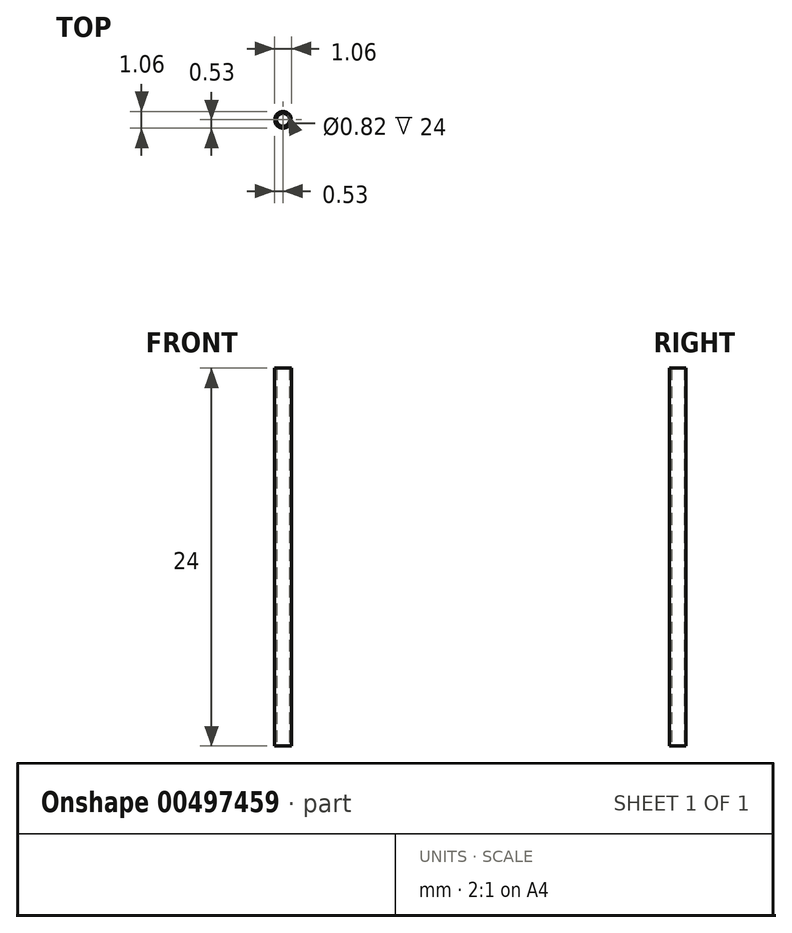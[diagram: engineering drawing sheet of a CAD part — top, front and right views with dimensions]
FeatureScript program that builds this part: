
annotation { "Feature Type Name" : "Feature", "Feature Type Description" : "" }
export const myFeature = defineFeature(function(context is Context, id is Id, definition is map)
    precondition{}
    {
        {
            var Q0;
            Q0=qCreatedBy(makeId("Top.planeOp"),FACE);
            var sketch = newSketch(context, id + "F0", { "sketchPlane" : qUnion([Q0])});
            skCircle(sketch, "E0", {"center": v(0, 0) * mm, "radius": 0.41 * mm});
            skCircle(sketch, "E1", {"center": v(0, 0) * mm, "radius": 0.53 * mm});
            skSolve(sketch);
        }
        {
            var Q0;
            Q0=makeQuery(id+"F0.imprint","IMPRINT",FACE,{"disambiguationData":[TD([[makeQuery(id+"F0.imprint","IMPRINT",EDGE,{"derivedFrom":sQuery(id+"F0.wireOp",EDGE,"E0")}),-1.0]])]});
            extrude(context, id + "F1", {"entities" : qUnion([Q0]), "depth" : 24 * mm});
        }
    });
